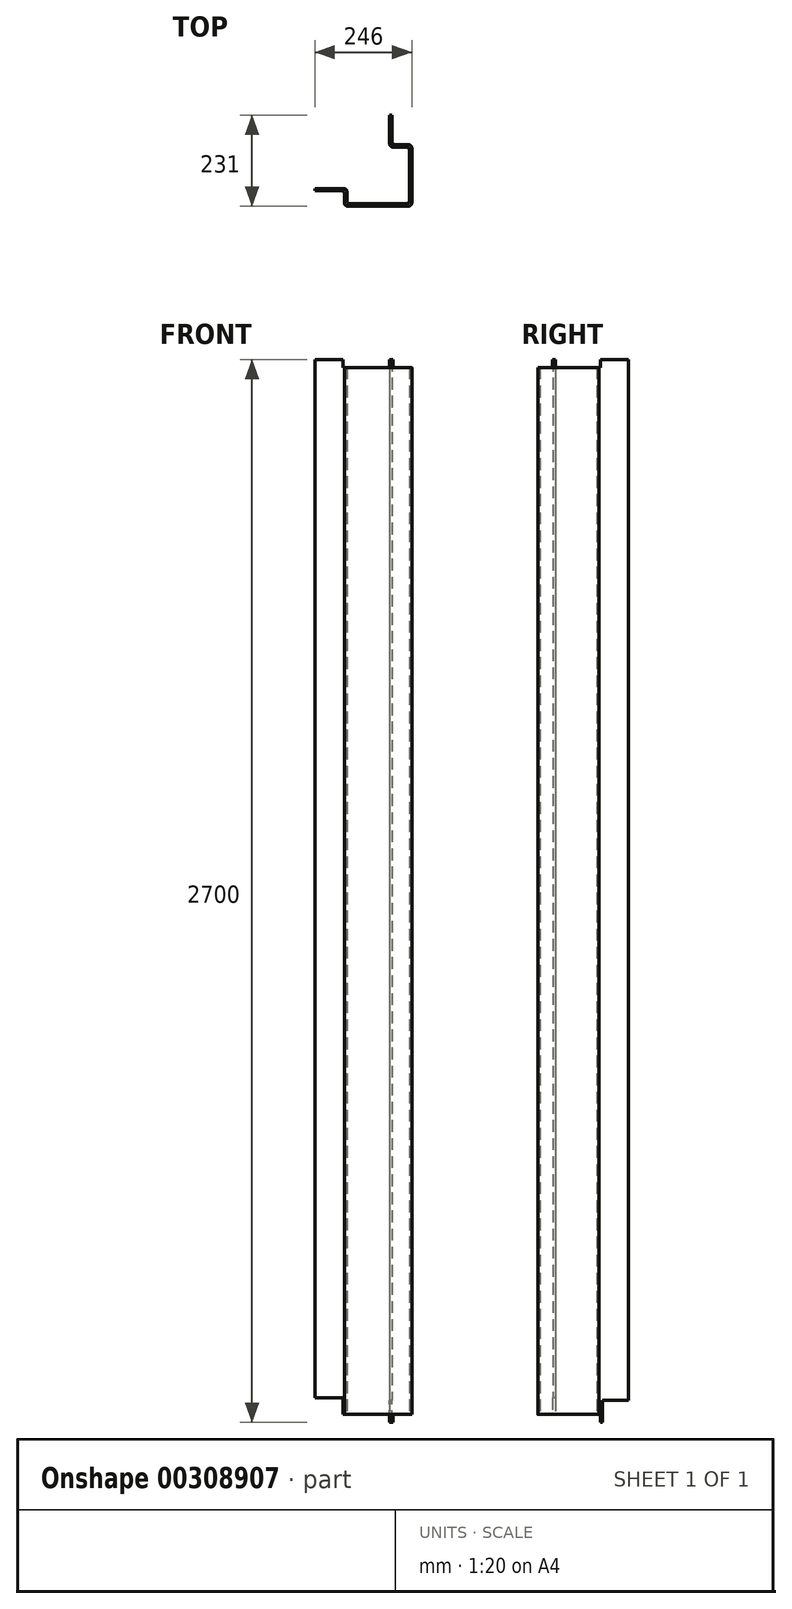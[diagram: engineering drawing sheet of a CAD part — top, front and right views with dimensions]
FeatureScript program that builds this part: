
annotation { "Feature Type Name" : "Feature", "Feature Type Description" : "" }
export const myFeature = defineFeature(function(context is Context, id is Id, definition is map)
    precondition{}
    {
        {
            var Q0;
            Q0=qCreatedBy(makeId("Top.planeOp"),FACE);
            var sketch = newSketch(context, id + "F0", { "sketchPlane" : qUnion([Q0])});
            skLineSegment(sketch, "E0", {"start": v(-44.59, 0) * mm, "end": v(-44.59, 6) * mm});
            skLineSegment(sketch, "E1", {"start": v(-44.59, 6) * mm, "end": v(28.41, 6) * mm});
            skLineSegment(sketch, "E2", {"start": v(-44.59, 0) * mm, "end": v(22.41, 0) * mm});
            skLineSegment(sketch, "E3", {"start": v(36.41, -2) * mm, "end": v(36.41, -25) * mm});
            skLineSegment(sketch, "E4", {"start": v(30.41, -8) * mm, "end": v(30.41, -31) * mm});
            skLineSegment(sketch, "E5", {"start": v(38.41, -39) * mm, "end": v(193.41, -39) * mm});
            skLineSegment(sketch, "E6", {"start": v(44.41, -33) * mm, "end": v(187.41, -33) * mm});
            skLineSegment(sketch, "E7", {"start": v(201.41, -31) * mm, "end": v(201.41, 109) * mm});
            skLineSegment(sketch, "E8", {"start": v(195.41, -25) * mm, "end": v(195.41, 103) * mm});
            skLineSegment(sketch, "E9", {"start": v(193.41, 117) * mm, "end": v(159.41, 117) * mm});
            skLineSegment(sketch, "E10", {"start": v(187.41, 111) * mm, "end": v(153.41, 111) * mm});
            skLineSegment(sketch, "E11", {"start": v(151.41, 125) * mm, "end": v(151.41, 192) * mm});
            skLineSegment(sketch, "E12", {"start": v(151.41, 192) * mm, "end": v(145.41, 192) * mm});
            skLineSegment(sketch, "E13", {"start": v(145.41, 192) * mm, "end": v(145.41, 119) * mm});
            skPoint(sketch, "E14.visualSharp", {"position": v(151.41, 117) * mm});
            skArc(sketch, "E14.filletArc", {"start": v(151.41, 125) * mm, "mid": v(153.75, 119.34) * mm, "end": v(159.41, 117) * mm});
            skPoint(sketch, "E15.visualSharp", {"position": v(145.41, 111) * mm});
            skArc(sketch, "E15.filletArc", {"start": v(145.41, 119) * mm, "mid": v(147.75, 113.34) * mm, "end": v(153.41, 111) * mm});
            skPoint(sketch, "E16.visualSharp", {"position": v(195.41, 111) * mm});
            skArc(sketch, "E16.filletArc", {"start": v(195.41, 103) * mm, "mid": v(193.07, 108.66) * mm, "end": v(187.41, 111) * mm});
            skPoint(sketch, "E17.visualSharp", {"position": v(195.41, -33) * mm});
            skArc(sketch, "E17.filletArc", {"start": v(187.41, -33) * mm, "mid": v(193.07, -30.66) * mm, "end": v(195.41, -25) * mm});
            skPoint(sketch, "E18.visualSharp", {"position": v(201.41, 117) * mm});
            skArc(sketch, "E18.filletArc", {"start": v(201.41, 109) * mm, "mid": v(199.07, 114.66) * mm, "end": v(193.41, 117) * mm});
            skPoint(sketch, "E19.visualSharp", {"position": v(201.41, -39) * mm});
            skArc(sketch, "E19.filletArc", {"start": v(193.41, -39) * mm, "mid": v(199.07, -36.66) * mm, "end": v(201.41, -31) * mm});
            skPoint(sketch, "E20.visualSharp", {"position": v(30.41, -39) * mm});
            skArc(sketch, "E20.filletArc", {"start": v(30.41, -31) * mm, "mid": v(32.75, -36.66) * mm, "end": v(38.41, -39) * mm});
            skPoint(sketch, "E21.visualSharp", {"position": v(36.41, -33) * mm});
            skArc(sketch, "E21.filletArc", {"start": v(36.41, -25) * mm, "mid": v(38.75, -30.66) * mm, "end": v(44.41, -33) * mm});
            skPoint(sketch, "E22.visualSharp", {"position": v(36.41, 6) * mm});
            skArc(sketch, "E22.filletArc", {"start": v(36.41, -2) * mm, "mid": v(34.07, 3.66) * mm, "end": v(28.41, 6) * mm});
            skPoint(sketch, "E23.visualSharp", {"position": v(30.41, 0) * mm});
            skArc(sketch, "E23.filletArc", {"start": v(30.41, -8) * mm, "mid": v(28.07, -2.34) * mm, "end": v(22.41, 0) * mm});
            skSolve(sketch);
        }
        {
            var Q0;
            Q0 = qSketchRegion(id + "F0", true);
            extrude(context, id + "F1", {"entities" : qUnion([Q0]), "depth" : 2700 * mm});
        }
        {
            var Q0;
            Q0=makeQuery(id+"F1.opExtrude","SWEPT_FACE",FACE,{"disambiguationData":[OSD([sQuery(id+"F0.wireOp",EDGE,"E5")])]});
            var sketch = newSketch(context, id + "F2", { "sketchPlane" : qUnion([Q0])});
            skLineSegment(sketch, "E24.0", {"start": v(38.41, 2700) * mm, "end": v(193.41, 2700) * mm});
            skLineSegment(sketch, "E25.0", {"start": v(38.41, 0) * mm, "end": v(193.41, 0) * mm});
            skLineSegment(sketch, "E26", {"start": v(193.41, 1350) * mm, "end": v(193.41, 2680) * mm});
            skLineSegment(sketch, "E27.0", {"start": v(201.41, 2700) * mm, "end": v(201.41, 0) * mm});
            skLineSegment(sketch, "E28", {"start": v(201.41, 2700) * mm, "end": v(26.41, 2700) * mm});
            skLineSegment(sketch, "E29", {"start": v(26.41, 2700) * mm, "end": v(26.41, 2680) * mm});
            skLineSegment(sketch, "E30", {"start": v(26.41, 2680) * mm, "end": v(193.41, 2680) * mm});
            skLineSegment(sketch, "E31", {"start": v(193.41, 1350) * mm, "end": v(93.35, 1350) * mm});
            skLineSegment(sketch, "E32.MirrorCS", {"start": v(26.41, 20) * mm, "end": v(193.41, 20) * mm});
            skLineSegment(sketch, "E33.MirrorCS", {"start": v(26.41, 0) * mm, "end": v(26.41, 20) * mm});
            skLineSegment(sketch, "E34.MirrorCS", {"start": v(201.41, 0) * mm, "end": v(26.41, 0) * mm});
            skLineSegment(sketch, "E35", {"start": v(193.41, 20) * mm, "end": v(201.41, 20) * mm});
            skLineSegment(sketch, "E36", {"start": v(193.41, 2680) * mm, "end": v(201.41, 2680) * mm});
            skSolve(sketch);
        }
        {
            var Q0;
            Q0 = qSketchRegion(id + "F2", true);
            extrude(context, id + "F3", {"entities" : qUnion([Q0]), "operationType" : NewBodyOperationType.REMOVE, "oppositeDirection" : true, "depth" : 159 * mm});
        }
        {
            var Q0;
            Q0=makeQuery(id+"F1.opExtrude","SWEPT_FACE",FACE,{"disambiguationData":[OSD([sQuery(id+"F0.wireOp",EDGE,"E1")])]});
            var sketch = newSketch(context, id + "F4", { "sketchPlane" : qUnion([Q0])});
            skLineSegment(sketch, "E37.bottom", {"start": v(44.59, 0) * mm, "end": v(-22.41, 0) * mm});
            skLineSegment(sketch, "E37.top", {"start": v(44.59, 56.32) * mm, "end": v(-22.41, 56.32) * mm});
            skLineSegment(sketch, "E37.left", {"start": v(44.59, 0) * mm, "end": v(44.59, 56.32) * mm});
            skLineSegment(sketch, "E37.right", {"start": v(-22.41, 0) * mm, "end": v(-22.41, 56.32) * mm});
            skSolve(sketch);
        }
        {
            var Q0;
            Q0=makeQuery(id+"F1.opExtrude","SWEPT_FACE",FACE,{"disambiguationData":[OSD([sQuery(id+"F0.wireOp",EDGE,"E13")])]});
            var sketch = newSketch(context, id + "F5", { "sketchPlane" : qUnion([Q0])});
            skLineSegment(sketch, "E38.bottom", {"start": v(-192, 0) * mm, "end": v(-125, 0) * mm});
            skLineSegment(sketch, "E38.top", {"start": v(-192, 56.32) * mm, "end": v(-125, 56.32) * mm});
            skLineSegment(sketch, "E38.left", {"start": v(-192, 0) * mm, "end": v(-192, 56.32) * mm});
            skLineSegment(sketch, "E38.right", {"start": v(-125, 0) * mm, "end": v(-125, 56.32) * mm});
            skSolve(sketch);
        }
        {
            var Q0;
            Q0=makeQuery(id+"F5.imprint","IMPRINT",FACE,{"disambiguationData":[TD([[makeQuery(id+"F5.imprint","IMPRINT",EDGE,{"derivedFrom":sQuery(id+"F5.wireOp",EDGE,"E38.bottom")}),1.0]])]});
            extrude(context, id + "F6", {"entities" : qUnion([Q0]), "operationType" : NewBodyOperationType.REMOVE, "oppositeDirection" : true, "depth" : 25 * mm});
        }
        {
            var Q0;
            Q0=qCreatedBy(makeId("Front.planeOp"),FACE);
            var sketch = newSketch(context, id + "F7", { "sketchPlane" : qUnion([Q0])});
            skLineSegment(sketch, "E39.0", {"start": v(-44.59, 0) * mm, "end": v(22.41, 0) * mm});
            skLineSegment(sketch, "E40.0", {"start": v(26.41, 0) * mm, "end": v(26.41, 20) * mm});
            skLineSegment(sketch, "E41.bottom", {"start": v(26.41, 0) * mm, "end": v(-44.59, 0) * mm});
            skLineSegment(sketch, "E41.top", {"start": v(26.41, 62) * mm, "end": v(-44.59, 62) * mm});
            skLineSegment(sketch, "E41.left", {"start": v(26.41, 0) * mm, "end": v(26.41, 62) * mm});
            skLineSegment(sketch, "E41.right", {"start": v(-44.59, 0) * mm, "end": v(-44.59, 62) * mm});
            skSolve(sketch);
        }
        {
            var Q0;
            Q0 = qSketchRegion(id + "F7", true);
            extrude(context, id + "F8", {"entities" : qUnion([Q0]), "operationType" : NewBodyOperationType.REMOVE, "endBound" : BoundingType.THROUGH_ALL, "oppositeDirection" : true, "depth" : 25 * mm, "hasSecondDirection" : true, "secondDirectionBound" : SecondDirectionBoundingType.THROUGH_ALL, "secondDirectionOppositeDirection" : false, "secondDirectionDepth" : 25 * mm});
        }
    });
